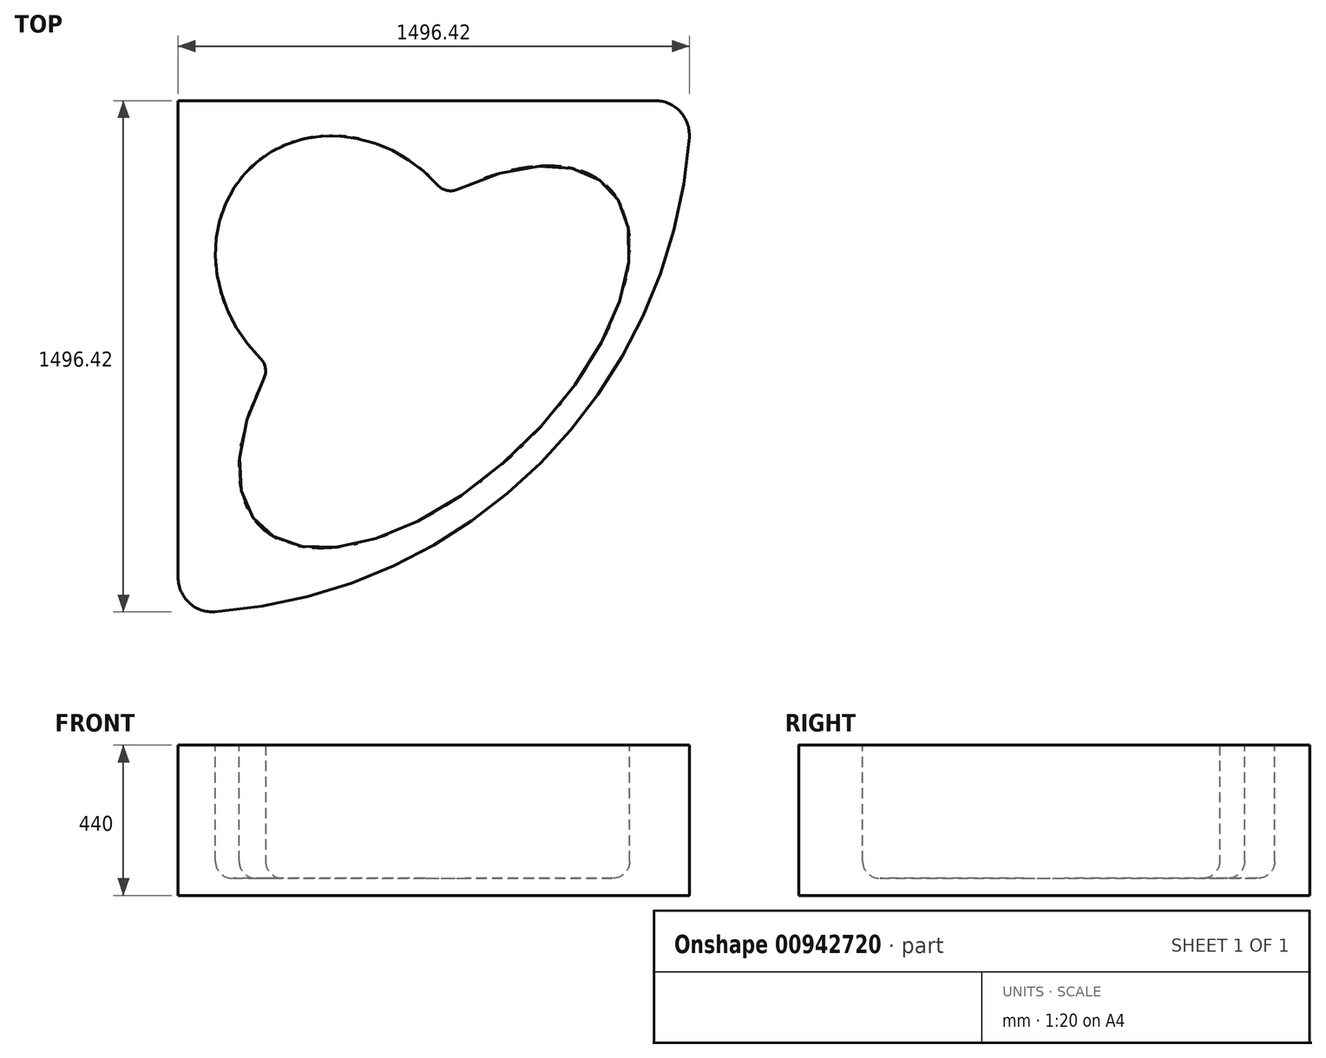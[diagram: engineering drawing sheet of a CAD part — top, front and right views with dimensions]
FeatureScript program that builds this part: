
annotation { "Feature Type Name" : "Feature", "Feature Type Description" : "" }
export const myFeature = defineFeature(function(context is Context, id is Id, definition is map)
    precondition{}
    {
        {
            var Q0;
            Q0=qCreatedBy(makeId("Top.planeOp"),FACE);
            var sketch = newSketch(context, id + "F0", { "sketchPlane" : qUnion([Q0])});
            skLineSegment(sketch, "E0.top", {"start": v(-750, 750) * mm, "end": v(646.42, 750) * mm});
            skLineSegment(sketch, "E0.left", {"start": v(-750, -646.42) * mm, "end": v(-750, 750) * mm});
            skLineSegment(sketch, "E1", {"start": v(-750, 0) * mm, "end": v(0, 0) * mm, "construction": true});
            skLineSegment(sketch, "E2", {"start": v(0, 0) * mm, "end": v(0, 750) * mm, "construction": true});
            skArc(sketch, "E3", {"start": v(-642.86, -746.17) * mm, "mid": v(310.66, -310.66) * mm, "end": v(746.17, 642.86) * mm});
            skLineSegment(sketch, "E4", {"start": v(-750, 750) * mm, "end": v(700.98, -700.98) * mm, "construction": true});
            skLineSegment(sketch, "E5", {"start": v(-849.05, -849.05) * mm, "end": v(849.05, 849.05) * mm, "construction": true});
            skEllipticalArc(sketch, "E6", {});
            skEllipticalArc(sketch, "E7", {});
            skPoint(sketch, "E8.visualSharp", {"position": v(34.25, 473.47) * mm});
            skArc(sketch, "E8.filletArc", {"start": v(10.3, 502.43) * mm, "mid": v(37.6, 486.85) * mm, "end": v(68.83, 490.66) * mm});
            skPoint(sketch, "E9.visualSharp", {"position": v(-481.82, -29.42) * mm});
            skArc(sketch, "E9.filletArc", {"start": v(-499.32, -62.7) * mm, "mid": v(-494.69, -32.17) * mm, "end": v(-508.87, -4.75) * mm});
            skPoint(sketch, "E10.visualSharp", {"position": v(750, 750) * mm});
            skArc(sketch, "E10.filletArc", {"start": v(746.17, 642.86) * mm, "mid": v(719.62, 718.14) * mm, "end": v(646.42, 750) * mm});
            skPoint(sketch, "E11.visualSharp", {"position": v(-750, -750) * mm});
            skArc(sketch, "E11.filletArc", {"start": v(-750, -646.42) * mm, "mid": v(-718.14, -719.62) * mm, "end": v(-642.86, -746.17) * mm});
            const initialGuessF0  = {"E6": [0, 0, 0.7204048446313156, 0.6935537901502161, 0.7111243014386722, 0.3655761625171016, 2.173628823295511, 0.9905155331792188], "E7": [-0.2585356701534204, 0.2585356701534203, -0.6558352514191672, 0.7549040488671113, 0.4070907673260117, 0.36296114984910494, 4.731578973989792, 1.6558292377155843]};
            skSetInitialGuess(sketch, initialGuessF0);
            skSolve(sketch);
        }
        {
            var Q0;
            Q0 = qSketchRegion(id + "F0", true);
            var Q1;
            Q1=makeQuery(id+"F0.imprint","IMPRINT",FACE,{"disambiguationData":[TD([[makeQuery(id+"F0.imprint","IMPRINT",EDGE,{"derivedFrom":sQuery(id+"F0.wireOp",EDGE,"E6")}),1.0]])]});
            extrude(context, id + "F1", {"entities" : qUnion([Q0, Q1]), "depth" : 440 * mm, "offsetDistance" : 25 * mm});
        }
        {
            var Q0;
            Q0=makeQuery(id+"F0.imprint","IMPRINT",FACE,{"disambiguationData":[TD([[makeQuery(id+"F0.imprint","IMPRINT",EDGE,{"derivedFrom":sQuery(id+"F0.wireOp",EDGE,"E6")}),1.0]])]});
            var Q1;
            Q1=makeQuery(id+"F1.opExtrude","CAP_FACE",FACE,{"disambiguationData":[OSD([sQuery(id+"F0.wireOp",EDGE,"E0.top"),sQuery(id+"F0.wireOp",EDGE,"E0.left"),sQuery(id+"F0.wireOp",EDGE,"E3"),sQuery(id+"F0.wireOp",EDGE,"E10.filletArc"),sQuery(id+"F0.wireOp",EDGE,"E11.filletArc")])],"isStart":false});
            extrude(context, id + "F2", {"entities" : qUnion([Q0]), "operationType" : NewBodyOperationType.REMOVE, "endBound" : BoundingType.UP_TO_SURFACE, "depth" : 25 * mm, "endBoundEntityFace" : qUnion([Q1]), "offsetDistance" : 25 * mm, "hasSecondDirection" : true, "secondDirectionOppositeDirection" : false, "secondDirectionDepth" : 50 * mm});
        }
        {
            var Q0;
            Q0=makeQuery(id+"F2.boolean.opBoolean","COPY",EDGE,{"derivedFrom":makeQuery(id+"F2.opExtrude","CAP_EDGE",EDGE,{"disambiguationData":[OSD([sQuery(id+"F0.wireOp",EDGE,"E6")])],"isStart":false})});
            var Q1;
            Q1=makeQuery(id+"F2.boolean.opBoolean","COPY",EDGE,{"derivedFrom":makeQuery(id+"F2.opExtrude","CAP_EDGE",EDGE,{"disambiguationData":[OSD([sQuery(id+"F0.wireOp",EDGE,"E7")])],"isStart":false})});
            var Q2;
            Q2=makeQuery(id+"F2.boolean.opBoolean","COPY",EDGE,{"derivedFrom":makeQuery(id+"F2.opExtrude","CAP_EDGE",EDGE,{"disambiguationData":[OSD([sQuery(id+"F0.wireOp",EDGE,"E6")])],"isStart":true})});
            fillet(context, id + "F3", {"entities" : qUnion([Q0, Q1, Q2]), "radius" : 50 * mm, "tangentPropagation" : true, "allowEdgeOverflow" : false});
        }
    });
